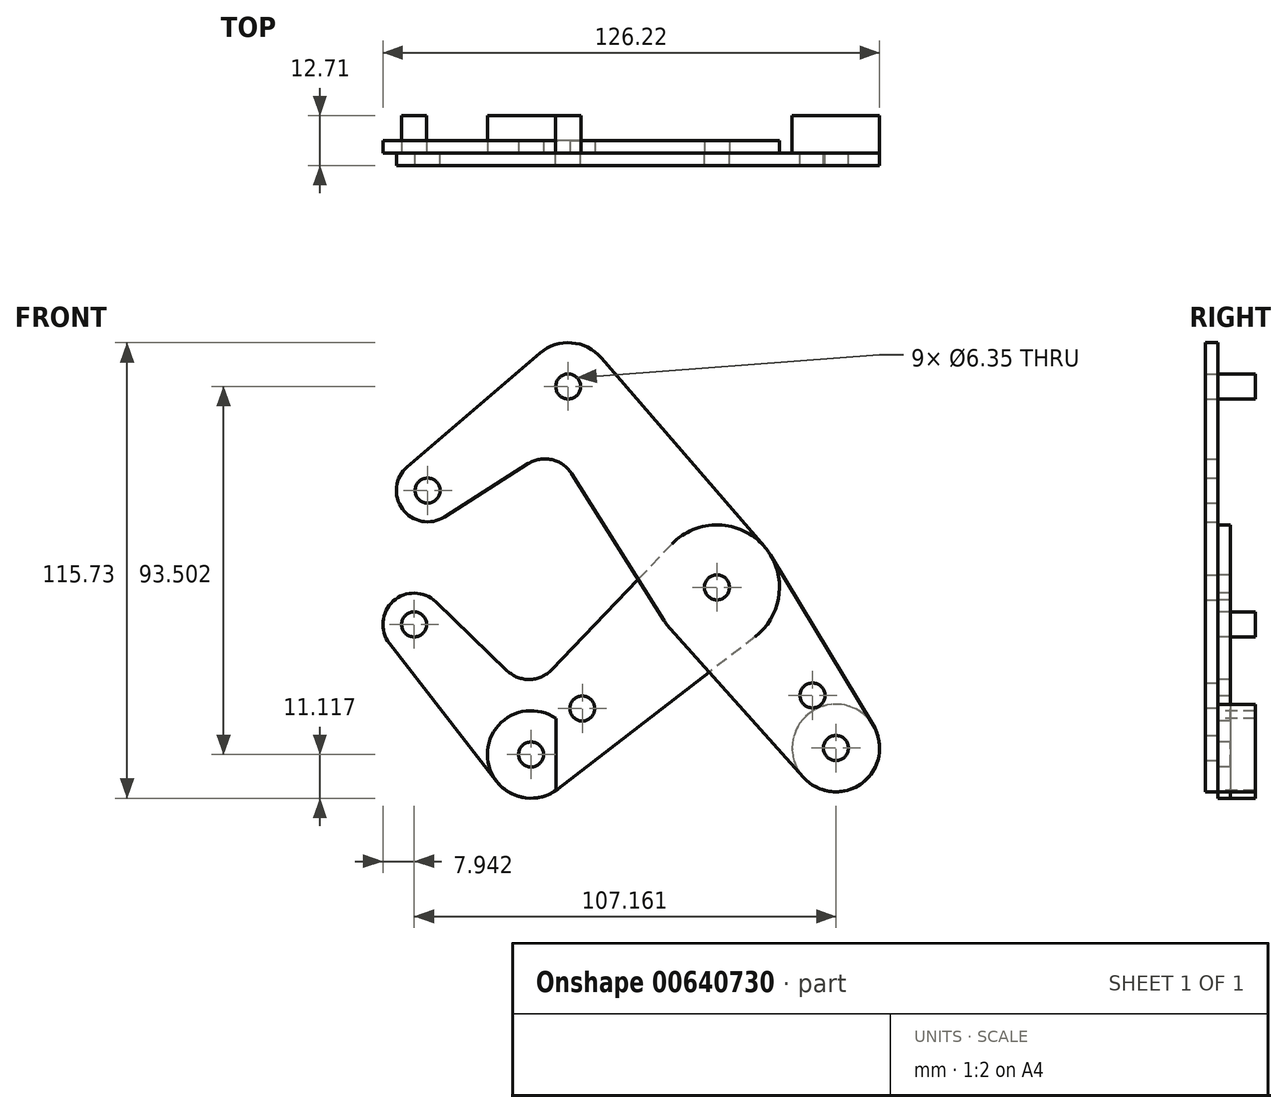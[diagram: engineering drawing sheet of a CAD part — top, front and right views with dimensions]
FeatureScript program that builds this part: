
annotation { "Feature Type Name" : "Feature", "Feature Type Description" : "" }
export const myFeature = defineFeature(function(context is Context, id is Id, definition is map)
    precondition{}
    {
        {
            var Q0;
            Q0=qCreatedBy(makeId("Front.planeOp"),FACE);
            var sketch = newSketch(context, id + "F0", { "sketchPlane" : qUnion([Q0])});
            skCircle(sketch, "E0", {"center": v(0, 0) * mm, "radius": 3.18 * mm});
            skCircle(sketch, "E1", {"center": v(0, 0) * mm, "radius": 15.88 * mm});
            skCircle(sketch, "E2", {"center": v(-37.78, 51.04) * mm, "radius": 3.18 * mm});
            skCircle(sketch, "E3", {"center": v(-37.78, 51.04) * mm, "radius": 11.11 * mm});
            skLineSegment(sketch, "E4", {"start": v(-37.78, 51.04) * mm, "end": v(-73.5, 24.6) * mm, "construction": true});
            skCircle(sketch, "E5", {"center": v(-73.5, 24.6) * mm, "radius": 3.18 * mm});
            skCircle(sketch, "E6", {"center": v(-73.5, 24.6) * mm, "radius": 7.94 * mm});
            skLineSegment(sketch, "E7", {"start": v(-78.67, 30.62) * mm, "end": v(-45.01, 59.48) * mm});
            skLineSegment(sketch, "E8", {"start": v(-13.43, -8.46) * mm, "end": v(-36.98, 28.93) * mm});
            skLineSegment(sketch, "E9", {"start": v(-69.25, 17.9) * mm, "end": v(-47.97, 31.4) * mm});
            skArc(sketch, "E10", {"start": v(-36.98, 28.93) * mm, "mid": v(-41.97, 32.45) * mm, "end": v(-47.97, 31.4) * mm});
            skCircle(sketch, "E11", {"center": v(-76.94, -9.41) * mm, "radius": 3.18 * mm});
            skCircle(sketch, "E12", {"center": v(-76.94, -9.41) * mm, "radius": 7.94 * mm});
            skLineSegment(sketch, "E13", {"start": v(-76.94, -9.41) * mm, "end": v(-47.21, -42.46) * mm, "construction": true});
            skCircle(sketch, "E14", {"center": v(-47.21, -42.46) * mm, "radius": 3.18 * mm});
            skCircle(sketch, "E15", {"center": v(-47.21, -42.46) * mm, "radius": 11.11 * mm});
            skLineSegment(sketch, "E16", {"start": v(-47.21, -42.46) * mm, "end": v(0, 0) * mm, "construction": true});
            skCircle(sketch, "E17", {"center": v(-34.22, -30.78) * mm, "radius": 3.18 * mm});
            skLineSegment(sketch, "E18", {"start": v(-83.2, -14.29) * mm, "end": v(-54.55, -51.13) * mm});
            skLineSegment(sketch, "E19", {"start": v(9.7, -12.57) * mm, "end": v(-40.42, -51.26) * mm});
            skLineSegment(sketch, "E20", {"start": v(-11.47, 10.97) * mm, "end": v(-42.02, -20.96) * mm});
            skLineSegment(sketch, "E21", {"start": v(-71.43, -3.7) * mm, "end": v(-53.28, -21.19) * mm});
            skArc(sketch, "E22", {"start": v(-53.28, -21.19) * mm, "mid": v(-47.6, -23.41) * mm, "end": v(-42.02, -20.96) * mm});
            skLineSegment(sketch, "E23", {"start": v(-29.37, 58.3) * mm, "end": v(12.02, 10.38) * mm});
            skLineSegment(sketch, "E24", {"start": v(-37.78, 51.04) * mm, "end": v(30.22, -40.83) * mm, "construction": true});
            skCircle(sketch, "E25", {"center": v(30.22, -40.83) * mm, "radius": 11.11 * mm});
            skCircle(sketch, "E26", {"center": v(30.22, -40.83) * mm, "radius": 3.18 * mm});
            skCircle(sketch, "E27", {"center": v(24.28, -27.47) * mm, "radius": 3.17 * mm});
            skLineSegment(sketch, "E28", {"start": v(24.28, -27.47) * mm, "end": v(21.73, -29.36) * mm, "construction": true});
            skLineSegment(sketch, "E29", {"start": v(13.59, 8.2) * mm, "end": v(39.74, -35.09) * mm});
            skLineSegment(sketch, "E30", {"start": v(-11.82, -10.6) * mm, "end": v(21.95, -48.25) * mm});
            skLineSegment(sketch, "E31", {"start": v(30.22, -40.83) * mm, "end": v(-47.21, -42.46) * mm, "construction": true});
            skArc(sketch, "E32", {"start": v(-40.86, -33.34) * mm, "mid": v(-58.32, -42.74) * mm, "end": v(-40.42, -51.26) * mm});
            skLineSegment(sketch, "E33", {"start": v(-40.86, -33.34) * mm, "end": v(-40.86, -51.58) * mm});
            skSolve(sketch);
        }
        {
            var Q0;
            Q0=makeQuery(id+"F0.imprint","IMPRINT",FACE,{"disambiguationData":[TD([[makeQuery(id+"F0.imprint","IMPRINT",EDGE,{"derivedFrom":sQuery(id+"F0.wireOp",EDGE,"E17")}),-1.0]])]});
            var Q1;
            {var subQ0=sQuery(id+"F0.wireOp",EDGE,"E19");var subQ1=sQuery(id+"F0.wireOp",EDGE,"E1");var subQ2=makeQuery(id+"F0.imprint","INTERSECT",VERTEX,{"derivedFrom":[subQ1,subQ0]});Q1=makeQuery(id+"F0.imprint","IMPRINT",FACE,{"disambiguationData":[TD([[makeQuery(id+"F0.imprint","IMPRINT",EDGE,{"disambiguationData":[TD([[subQ2,1.0]])],"derivedFrom":subQ1}),-1.0]])]});}
            var Q2;
            {var subQ0=sQuery(id+"F0.wireOp",EDGE,"E8");var subQ1=sQuery(id+"F0.wireOp",EDGE,"E1");var subQ2=makeQuery(id+"F0.imprint","INTERSECT",VERTEX,{"derivedFrom":[subQ1,subQ0]});Q2=makeQuery(id+"F0.imprint","IMPRINT",FACE,{"disambiguationData":[TD([[makeQuery(id+"F0.imprint","IMPRINT",EDGE,{"disambiguationData":[TD([[subQ2,1.0]])],"derivedFrom":subQ1}),-1.0]])]});}
            var Q3;
            Q3=makeQuery(id+"F0.imprint","IMPRINT",FACE,{"disambiguationData":[TD([[makeQuery(id+"F0.imprint","IMPRINT",EDGE,{"derivedFrom":sQuery(id+"F0.wireOp",EDGE,"E0")}),-1.0]])]});
            var Q4;
            Q4=makeQuery(id+"F0.imprint","IMPRINT",FACE,{"disambiguationData":[TD([[makeQuery(id+"F0.imprint","IMPRINT",EDGE,{"derivedFrom":sQuery(id+"F0.wireOp",EDGE,"E14")}),-1.0]])]});
            var Q5;
            Q5=makeQuery(id+"F0.imprint","IMPRINT",FACE,{"disambiguationData":[TD([[makeQuery(id+"F0.imprint","IMPRINT",EDGE,{"derivedFrom":sQuery(id+"F0.wireOp",EDGE,"E11")}),-1.0]])]});
            var Q6;
            Q6=qCreatedBy(id+"FdfClBeGEtfWta8_1.planeOp",FACE);
            extrude(context, id + "F1", {"entities" : qUnion([Q0, Q1, Q2, Q3, Q4, Q5]), "oppositeDirection" : true, "depth" : 3.17 * mm, "endBoundEntityFace" : qUnion([Q6]), "offsetDistance" : 25.4 * mm});
        }
        {
            var Q0;
            Q0=makeQuery(id+"F0.imprint","IMPRINT",FACE,{"disambiguationData":[TD([[makeQuery(id+"F0.imprint","IMPRINT",EDGE,{"derivedFrom":sQuery(id+"F0.wireOp",EDGE,"E5")}),-1.0]])]});
            var Q1;
            {var subQ0=sQuery(id+"F0.wireOp",EDGE,"E7");Q1=makeQuery(id+"F0.imprint","IMPRINT",FACE,{"disambiguationData":[TD([[makeQuery(id+"F0.imprint","IMPRINT",EDGE,{"derivedFrom":subQ0}),-1.0]])]});}
            var Q2;
            Q2=makeQuery(id+"F0.imprint","IMPRINT",FACE,{"disambiguationData":[TD([[makeQuery(id+"F0.imprint","IMPRINT",EDGE,{"derivedFrom":sQuery(id+"F0.wireOp",EDGE,"E2")}),-1.0]])]});
            var Q3;
            Q3=makeQuery(id+"F0.imprint","IMPRINT",FACE,{"disambiguationData":[TD([[makeQuery(id+"F0.imprint","IMPRINT",EDGE,{"derivedFrom":sQuery(id+"F0.wireOp",EDGE,"E0")}),-1.0]])]});
            var Q4;
            {var subQ0=sQuery(id+"F0.wireOp",EDGE,"E8");var subQ1=sQuery(id+"F0.wireOp",EDGE,"E1");var subQ2=makeQuery(id+"F0.imprint","INTERSECT",VERTEX,{"derivedFrom":[subQ1,subQ0]});Q4=makeQuery(id+"F0.imprint","IMPRINT",FACE,{"disambiguationData":[TD([[makeQuery(id+"F0.imprint","IMPRINT",EDGE,{"disambiguationData":[TD([[subQ2,1.0]])],"derivedFrom":subQ1}),-1.0]])]});}
            var Q5;
            {var subQ0=sQuery(id+"F0.wireOp",EDGE,"E19");var subQ1=sQuery(id+"F0.wireOp",EDGE,"E1");var subQ2=makeQuery(id+"F0.imprint","INTERSECT",VERTEX,{"derivedFrom":[subQ1,subQ0]});Q5=makeQuery(id+"F0.imprint","IMPRINT",FACE,{"disambiguationData":[TD([[makeQuery(id+"F0.imprint","IMPRINT",EDGE,{"disambiguationData":[TD([[subQ2,1.0]])],"derivedFrom":subQ1}),-1.0]])]});}
            var Q6;
            Q6=makeQuery(id+"F0.imprint","IMPRINT",FACE,{"disambiguationData":[TD([[makeQuery(id+"F0.imprint","IMPRINT",EDGE,{"derivedFrom":sQuery(id+"F0.wireOp",EDGE,"E27")}),-1.0]])]});
            var Q7;
            Q7=makeQuery(id+"F0.imprint","IMPRINT",FACE,{"disambiguationData":[TD([[makeQuery(id+"F0.imprint","IMPRINT",EDGE,{"derivedFrom":sQuery(id+"F0.wireOp",EDGE,"E26")}),-1.0]])]});
            extrude(context, id + "F2", {"entities" : qUnion([Q0, Q1, Q2, Q3, Q4, Q5, Q6, Q7]), "depth" : 3.17 * mm, "offsetDistance" : 25.4 * mm});
        }
        {
            var Q0;
            {var subQ2=sQuery(id+"F0.wireOp",EDGE,"E33");Q0=makeQuery(id+"F0.imprint","IMPRINT",FACE,{"disambiguationData":[TD([[makeQuery(id+"F0.imprint","IMPRINT",EDGE,{"derivedFrom":subQ2}),1.0]])]});}
            extrude(context, id + "F3", {"entities" : qUnion([Q0]), "operationType" : NewBodyOperationType.ADD, "oppositeDirection" : true, "depth" : 3.17 * mm, "offsetDistance" : 25.4 * mm});
        }
        {
            var Q0;
            Q0=qCreatedBy(makeId("Front.planeOp"),FACE);
            cPlane(context, id + "F4", {"entities" : qUnion([Q0]), "cplaneType" : CPlaneType.OFFSET, "offset" : 9.52 * mm, "oppositeDirection" : true, "width" : 152.4 * mm, "height" : 152.4 * mm});
        }
        {
            var Q0;
            Q0=qCreatedBy(makeId("Front.planeOp"),FACE);
            var sketch = newSketch(context, id + "F5", { "sketchPlane" : qUnion([Q0])});
            skCircle(sketch, "E34", {"center": v(-37.78, 51.04) * mm, "radius": 3.2 * mm});
            skCircle(sketch, "E35", {"center": v(-76.94, -9.41) * mm, "radius": 3.15 * mm});
            skCircle(sketch, "E36", {"center": v(30.22, -40.83) * mm, "radius": 11.1 * mm});
            skSolve(sketch);
        }
        {
            var Q0;
            Q0=makeQuery(id+"F0.imprint","IMPRINT",FACE,{"disambiguationData":[TD([[makeQuery(id+"F0.imprint","IMPRINT",EDGE,{"derivedFrom":sQuery(id+"F0.wireOp",EDGE,"E26")}),-1.0]])]});
            var Q1;
            Q1=makeQuery(id+"F0.imprint","IMPRINT",FACE,{"disambiguationData":[TD([[makeQuery(id+"F0.imprint","IMPRINT",EDGE,{"derivedFrom":sQuery(id+"F0.wireOp",EDGE,"E26")}),1.0]])]});
            var Q2;
            Q2=makeQuery(id+"F0.imprint","IMPRINT",FACE,{"disambiguationData":[TD([[makeQuery(id+"F0.imprint","IMPRINT",EDGE,{"derivedFrom":sQuery(id+"F0.wireOp",EDGE,"E14")}),1.0]])]});
            var Q3;
            Q3=makeQuery(id+"F0.imprint","IMPRINT",FACE,{"disambiguationData":[TD([[makeQuery(id+"F0.imprint","IMPRINT",EDGE,{"derivedFrom":sQuery(id+"F0.wireOp",EDGE,"E14")}),-1.0]])]});
            var Q4;
            Q4=makeQuery(id+"F5.imprint","IMPRINT",FACE,{"disambiguationData":[TD([[makeQuery(id+"F5.imprint","IMPRINT",EDGE,{"derivedFrom":sQuery(id+"F5.wireOp",EDGE,"E34")}),1.0]])]});
            var Q5;
            Q5=qCreatedBy(id+"F4.planeOp",FACE);
            extrude(context, id + "F6", {"entities" : qUnion([Q0, Q1, Q2, Q3, Q4]), "endBound" : BoundingType.UP_TO_SURFACE, "oppositeDirection" : true, "depth" : 25.4 * mm, "endBoundEntityFace" : qUnion([Q5]), "offsetDistance" : 25.4 * mm});
        }
        {
            var Q0;
            Q0=makeQuery(id+"F0.imprint","IMPRINT",FACE,{"disambiguationData":[TD([[makeQuery(id+"F0.imprint","IMPRINT",EDGE,{"derivedFrom":sQuery(id+"F0.wireOp",EDGE,"E11")}),1.0]])]});
            var Q1;
            Q1=qCreatedBy(id+"F4.planeOp",FACE);
            extrude(context, id + "F7", {"entities" : qUnion([Q0]), "endBound" : BoundingType.UP_TO_SURFACE, "oppositeDirection" : true, "depth" : 25.4 * mm, "endBoundEntityFace" : qUnion([Q1]), "offsetDistance" : 25.4 * mm});
        }
    });
